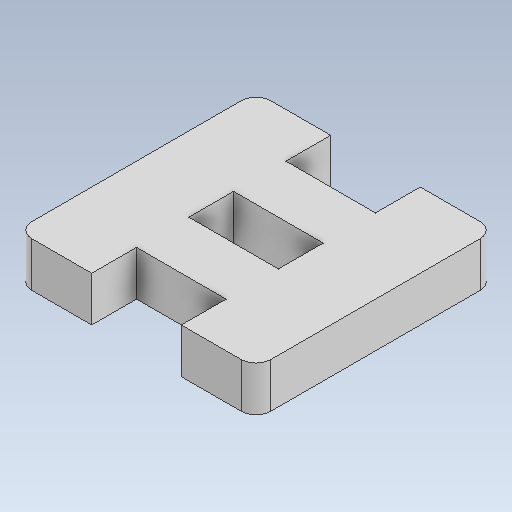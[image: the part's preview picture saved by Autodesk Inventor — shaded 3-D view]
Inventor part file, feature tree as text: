
AUTODESK INVENTOR PART (.ipt)
format: ipt  version: 2020 (Build 240168000, 168)  size: 111,616 bytes
history: native  units: mm
features: other x1, extrude x1, fillet x1, sketch x1
ambient origin geometry x8: Origin, YZ Plane, XZ Plane, XY Plane, X Axis, Y Axis, Z Axis, Center Point
bodies: Body1 (feature_tree)
feature tree (4):
  other  "Bryła1"
  extrude  "Wyciągnięcie proste1"  Depth=3.0mm TaperAngle=0.0deg
  fillet  "Zaokrąglenie1"  Radius=1.0mm
  sketch  "Szkic1"
